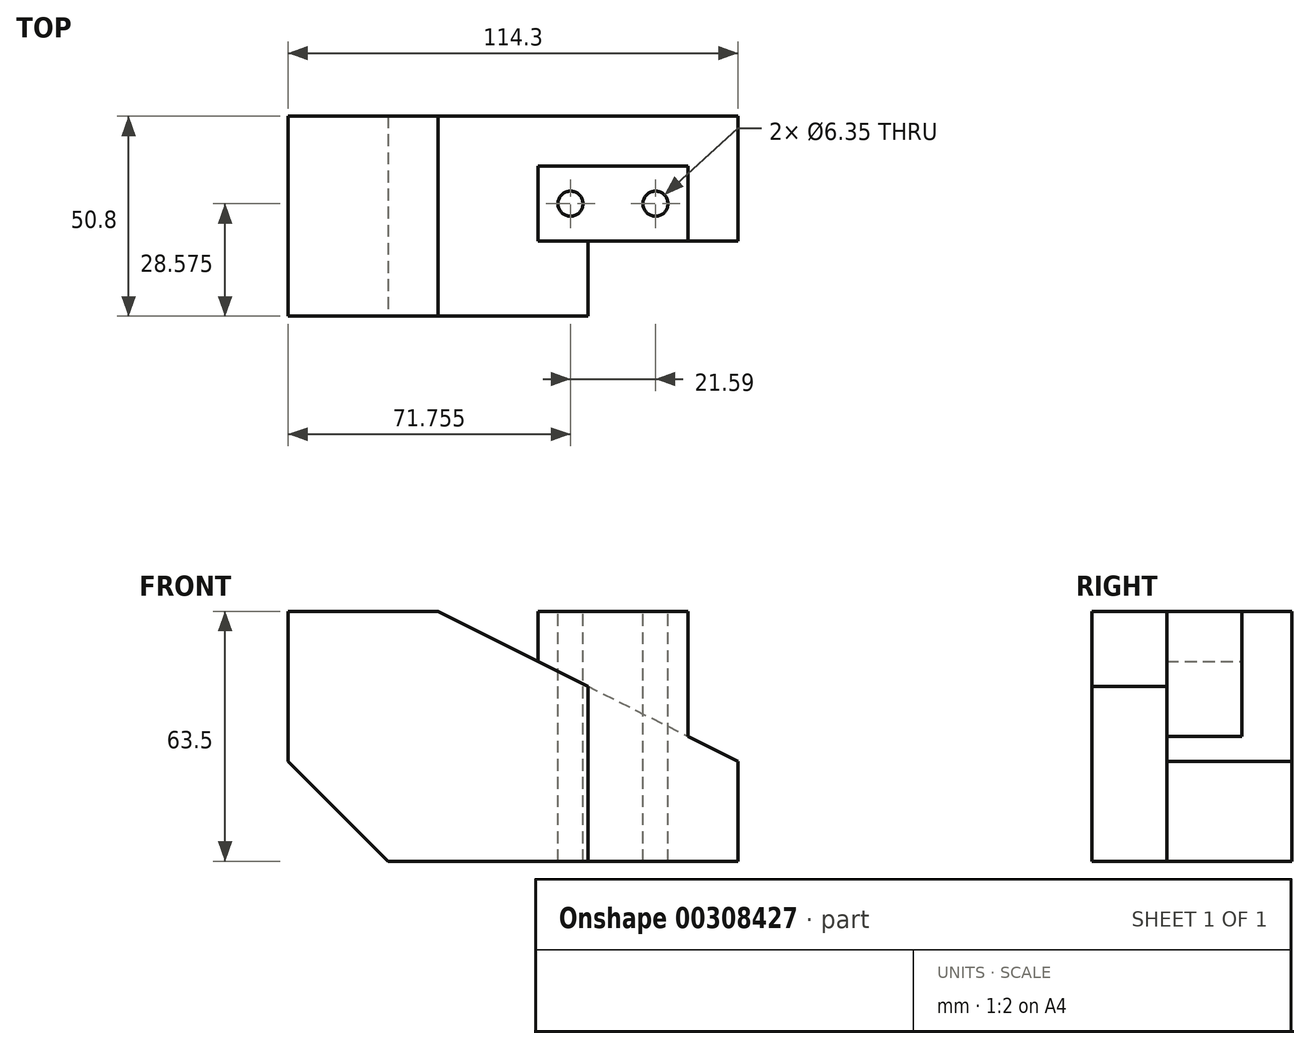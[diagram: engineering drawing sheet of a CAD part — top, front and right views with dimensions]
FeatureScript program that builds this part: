
annotation { "Feature Type Name" : "Feature", "Feature Type Description" : "" }
export const myFeature = defineFeature(function(context is Context, id is Id, definition is map)
    precondition{}
    {
        {
            var Q0;
            Q0=qCreatedBy(makeId("Front.planeOp"),FACE);
            var sketch = newSketch(context, id + "F0", { "sketchPlane" : qUnion([Q0])});
            skLineSegment(sketch, "E0", {"start": v(0, 0) * mm, "end": v(114.3, 0) * mm});
            skLineSegment(sketch, "E1", {"start": v(0, 0) * mm, "end": v(0, 63.5) * mm});
            skLineSegment(sketch, "E2", {"start": v(0, 63.5) * mm, "end": v(114.3, 63.5) * mm});
            skLineSegment(sketch, "E3", {"start": v(114.3, 63.5) * mm, "end": v(114.3, 0) * mm});
            skSolve(sketch);
        }
        {
            var Q0;
            Q0 = qSketchRegion(id + "F0", true);
            extrude(context, id + "F1", {"entities" : qUnion([Q0]), "depth" : 50.8 * mm});
        }
        {
            var Q0;
            Q0=makeQuery(id+"F1.opExtrude","CAP_FACE",FACE,{"disambiguationData":[OSD([sQuery(id+"F0.wireOp",EDGE,"E0"),sQuery(id+"F0.wireOp",EDGE,"E1"),sQuery(id+"F0.wireOp",EDGE,"E2"),sQuery(id+"F0.wireOp",EDGE,"E3")])],"isStart":false});
            var sketch = newSketch(context, id + "F2", { "sketchPlane" : qUnion([Q0])});
            skLineSegment(sketch, "E4", {"start": v(114.3, 0) * mm, "end": v(76.2, 0) * mm});
            skLineSegment(sketch, "E5", {"start": v(76.2, 0) * mm, "end": v(76.2, 63.5) * mm});
            skLineSegment(sketch, "E6", {"start": v(76.2, 63.5) * mm, "end": v(114.3, 63.5) * mm});
            skLineSegment(sketch, "E7", {"start": v(114.3, 63.5) * mm, "end": v(114.3, 0) * mm});
            skSolve(sketch);
        }
        {
            var Q0;
            Q0 = qSketchRegion(id + "F2", true);
            extrude(context, id + "F3", {"entities" : qUnion([Q0]), "operationType" : NewBodyOperationType.REMOVE, "oppositeDirection" : true, "depth" : 19.05 * mm});
        }
        {
            var Q0;
            Q0=makeQuery(id+"F1.opExtrude","CAP_FACE",FACE,{"disambiguationData":[OSD([sQuery(id+"F0.wireOp",EDGE,"E0"),sQuery(id+"F0.wireOp",EDGE,"E1"),sQuery(id+"F0.wireOp",EDGE,"E2"),sQuery(id+"F0.wireOp",EDGE,"E3")])],"isStart":false});
            var sketch = newSketch(context, id + "F4", { "sketchPlane" : qUnion([Q0])});
            skLineSegment(sketch, "E8", {"start": v(76.2, 63.5) * mm, "end": v(38.1, 63.5) * mm});
            skLineSegment(sketch, "E9", {"start": v(76.2, 44.45) * mm, "end": v(38.1, 63.5) * mm});
            skLineSegment(sketch, "E10", {"start": v(76.2, 63.5) * mm, "end": v(76.2, 44.45) * mm});
            skSolve(sketch);
        }
        {
            var Q0;
            Q0 = qSketchRegion(id + "F4", true);
            extrude(context, id + "F5", {"entities" : qUnion([Q0]), "operationType" : NewBodyOperationType.REMOVE, "oppositeDirection" : true, "depth" : 19.05 * mm});
        }
        {
            var Q0;
            Q0=makeQuery(id+"F1.opExtrude","CAP_FACE",FACE,{"disambiguationData":[OSD([sQuery(id+"F0.wireOp",EDGE,"E0"),sQuery(id+"F0.wireOp",EDGE,"E1"),sQuery(id+"F0.wireOp",EDGE,"E2"),sQuery(id+"F0.wireOp",EDGE,"E3")])],"isStart":true});
            var sketch = newSketch(context, id + "F6", { "sketchPlane" : qUnion([Q0])});
            skLineSegment(sketch, "E11", {"start": v(-114.3, 0) * mm, "end": v(-114.3, 25.4) * mm});
            skLineSegment(sketch, "E12", {"start": v(-114.3, 25.4) * mm, "end": v(-114.3, 63.5) * mm});
            skLineSegment(sketch, "E13", {"start": v(-114.3, 63.5) * mm, "end": v(-38.1, 63.5) * mm});
            skLineSegment(sketch, "E14", {"start": v(-38.1, 63.5) * mm, "end": v(-114.3, 25.4) * mm});
            skSolve(sketch);
        }
        {
            var Q0;
            Q0 = qSketchRegion(id + "F6", true);
            extrude(context, id + "F7", {"entities" : qUnion([Q0]), "operationType" : NewBodyOperationType.REMOVE, "oppositeDirection" : true, "depth" : 12.7 * mm});
        }
        {
            var Q0;
            Q0=makeQuery(id+"F7.boolean.opBoolean","COPY",FACE,{"derivedFrom":makeQuery(id+"F7.opExtrude","CAP_FACE",FACE,{"disambiguationData":[OSD([sQuery(id+"F6.wireOp",EDGE,"E12"),sQuery(id+"F6.wireOp",EDGE,"E13"),sQuery(id+"F6.wireOp",EDGE,"E14")])],"isStart":false})});
            var sketch = newSketch(context, id + "F8", { "sketchPlane" : qUnion([Q0])});
            skLineSegment(sketch, "E15", {"start": v(-114.3, 63.5) * mm, "end": v(-101.6, 63.5) * mm});
            skLineSegment(sketch, "E16", {"start": v(-101.6, 63.5) * mm, "end": v(-101.6, 31.75) * mm});
            skLineSegment(sketch, "E17", {"start": v(-101.6, 31.75) * mm, "end": v(-114.3, 25.4) * mm});
            skLineSegment(sketch, "E18", {"start": v(-114.3, 25.4) * mm, "end": v(-114.3, 63.5) * mm});
            skSolve(sketch);
        }
        {
            var Q0;
            Q0 = qSketchRegion(id + "F8", true);
            extrude(context, id + "F9", {"entities" : qUnion([Q0]), "operationType" : NewBodyOperationType.REMOVE, "oppositeDirection" : true, "depth" : 25.4 * mm});
        }
        {
            var Q0;
            Q0=makeQuery(id+"F7.boolean.opBoolean","COPY",FACE,{"derivedFrom":makeQuery(id+"F7.opExtrude","CAP_FACE",FACE,{"disambiguationData":[OSD([sQuery(id+"F6.wireOp",EDGE,"E12"),sQuery(id+"F6.wireOp",EDGE,"E13"),sQuery(id+"F6.wireOp",EDGE,"E14")])],"isStart":false})});
            var sketch = newSketch(context, id + "F10", { "sketchPlane" : qUnion([Q0])});
            skLineSegment(sketch, "E19", {"start": v(-38.1, 63.5) * mm, "end": v(-63.5, 63.5) * mm});
            skLineSegment(sketch, "E20", {"start": v(-63.5, 63.5) * mm, "end": v(-63.5, 50.8) * mm});
            skLineSegment(sketch, "E21", {"start": v(-63.5, 50.8) * mm, "end": v(-38.1, 63.5) * mm});
            skSolve(sketch);
        }
        {
            var Q0;
            Q0 = qSketchRegion(id + "F10", true);
            extrude(context, id + "F11", {"entities" : qUnion([Q0]), "operationType" : NewBodyOperationType.REMOVE, "oppositeDirection" : true, "depth" : 25.4 * mm});
        }
        {
            var Q0;
            Q0=makeQuery(id+"F1.opExtrude","CAP_FACE",FACE,{"disambiguationData":[OSD([sQuery(id+"F0.wireOp",EDGE,"E0"),sQuery(id+"F0.wireOp",EDGE,"E1"),sQuery(id+"F0.wireOp",EDGE,"E2"),sQuery(id+"F0.wireOp",EDGE,"E3")])],"isStart":false});
            var sketch = newSketch(context, id + "F12", { "sketchPlane" : qUnion([Q0])});
            skLineSegment(sketch, "E22", {"start": v(0, 0) * mm, "end": v(0, 25.4) * mm});
            skLineSegment(sketch, "E23", {"start": v(0, 25.4) * mm, "end": v(0, 0) * mm});
            skLineSegment(sketch, "E24", {"start": v(0, 0) * mm, "end": v(25.4, 0) * mm});
            skLineSegment(sketch, "E25", {"start": v(25.4, 0) * mm, "end": v(0, 25.4) * mm});
            skSolve(sketch);
        }
        {
            var Q0;
            Q0 = qSketchRegion(id + "F12", true);
            extrude(context, id + "F13", {"entities" : qUnion([Q0]), "operationType" : NewBodyOperationType.REMOVE, "oppositeDirection" : true, "depth" : 127 * mm});
        }
        {
            var Q0;
            Q0=makeQuery(id+"F11.boolean.opBoolean","SPLIT",FACE,{"disambiguationData":[TD([makeQuery(id+"F9.boolean.opBoolean","COPY",FACE,{"derivedFrom":makeQuery(id+"F9.opExtrude","SWEPT_FACE",FACE,{"disambiguationData":[OSD([sQuery(id+"F8.wireOp",EDGE,"E16")])]})})])],"derivedFrom":makeQuery(id+"F1.opExtrude","SWEPT_FACE",FACE,{"disambiguationData":[OSD([sQuery(id+"F0.wireOp",EDGE,"E2")])]})});
            var sketch = newSketch(context, id + "F14", { "sketchPlane" : qUnion([Q0])});
            skLineSegment(sketch, "E26", {"start": v(63.5, -12.7) * mm, "end": v(63.5, -19.05) * mm});
            skLineSegment(sketch, "E27", {"start": v(63.5, -19.05) * mm, "end": v(63.5, -25.4) * mm});
            skLineSegment(sketch, "E28", {"start": v(63.5, -25.4) * mm, "end": v(63.5, -22.23) * mm});
            skLineSegment(sketch, "E29", {"start": v(63.5, -22.23) * mm, "end": v(71.76, -22.23) * mm});
            skCircle(sketch, "E30", {"center": v(71.76, -22.23) * mm, "radius": 3.18 * mm});
            skLineSegment(sketch, "E31", {"start": v(101.6, -12.7) * mm, "end": v(101.6, -22.23) * mm});
            skLineSegment(sketch, "E32", {"start": v(101.6, -22.23) * mm, "end": v(93.35, -22.23) * mm});
            skCircle(sketch, "E33", {"center": v(93.35, -22.23) * mm, "radius": 3.18 * mm});
            skSolve(sketch);
        }
        {
            var Q0;
            Q0 = qSketchRegion(id + "F14", true);
            extrude(context, id + "F15", {"entities" : qUnion([Q0]), "operationType" : NewBodyOperationType.REMOVE, "oppositeDirection" : true, "depth" : 228.6 * mm});
        }
    });
